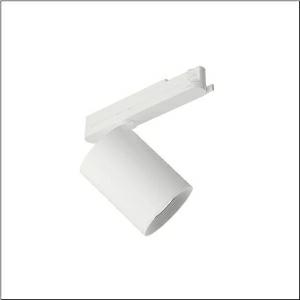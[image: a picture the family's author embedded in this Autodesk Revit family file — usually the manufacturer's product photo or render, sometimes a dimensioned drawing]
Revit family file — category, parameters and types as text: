
# Revit family: spot_21_51se12mbd5b
name_source: partatom
category: Lighting Fixtures
units: mm (PartAtom-declared; Revit-internal decimal feet)

## family parameters
Cut with Voids When Loaded = No
Host = Face
Light Source = No
Part Type = Normal
Room Calculation Point = No
Round Connector Dimension = Use Diameter
Shared = No

## types (1)
- --- (1 x LED, 5460 lm, 41.5 W, 4000K)
    Apparent Load = 42 VA
    CIE Flux Codes = 95 98 99 100 100
    Color Rendering = 90
    Color Temperature = 4000K
    Default Elevation = 1800 mm
    Description = Spot 21, directional spotlight, light control with lens, of PMMA, LED rated luminous flux: 5.250lm, light colour: 940, control gear: ECG Multilumen, with 3-phase adapter, mains connection: 220..240V, AC, 50/60Hz, of aluminium, traffic white (RAL 9016), length: 213mm, diameter: 105mm, protection rating (complete): IP20, insulation class (complete): insulation class I (protective earthing), certification: CE, impact resistance: IK02, permissible ambient temperature for indoor applications: -20..+40°C, packaging unit: 1 piece
    Height = 175 mm
    Lamp = 1 x LED
    Lamp Light Flux = 5460 lm
    Lamp Power = 41.5 W
    Lamp count = 1
    Length = 105 mm
    Luminous efficacy = 132 lm/W
    Manufacturer = Siteco
    ModVariant = No
    Model = 51SE12MBD5B
    Mounting Place = Ceiling
    Mounting Type = Pendant
    Number of Poles = 1
    OnlyDefault = Yes
    Power Factor = 1
    Product Name = Spot 21
    Product group = directional spotlight
    ProductGroupID = 906
    Protection Class = Protection class I
    Protection Degree = IP 20
    RLX_Detail_Level = 1
    RLX_Emergency_Light_Flux = 0 lm
    RLX_Emergency_Type = 0
    RLX_Emergency_Type_DB = No
    RlxData = <blob elided: 17629 chars, md5=55a4b2c5>
    Socket = socket
    Standby Power = 0 W
    System Light Flux = 5460 lm
    System Power = 42 W
    Type Comments = factory setting: luminous flux: 100 % | (ON | ON | ON | ON) | 1050 mA
    Type Image = l_1003976.jpg
    URL = http://relux.com
    VarID = @adj_144474
    Voltage = 0 V
    Weight = 0.00 kg
    Width = 0 mm  [stored 0 ft]

note: [stored X ft] marks values corroborated as IEEE doubles in the binary element streams (Revit-internal decimal feet)

## geometry (parser evidence)
native form markers: Blend x4, Sweep x11
no freeform markers — native parametric forms only
